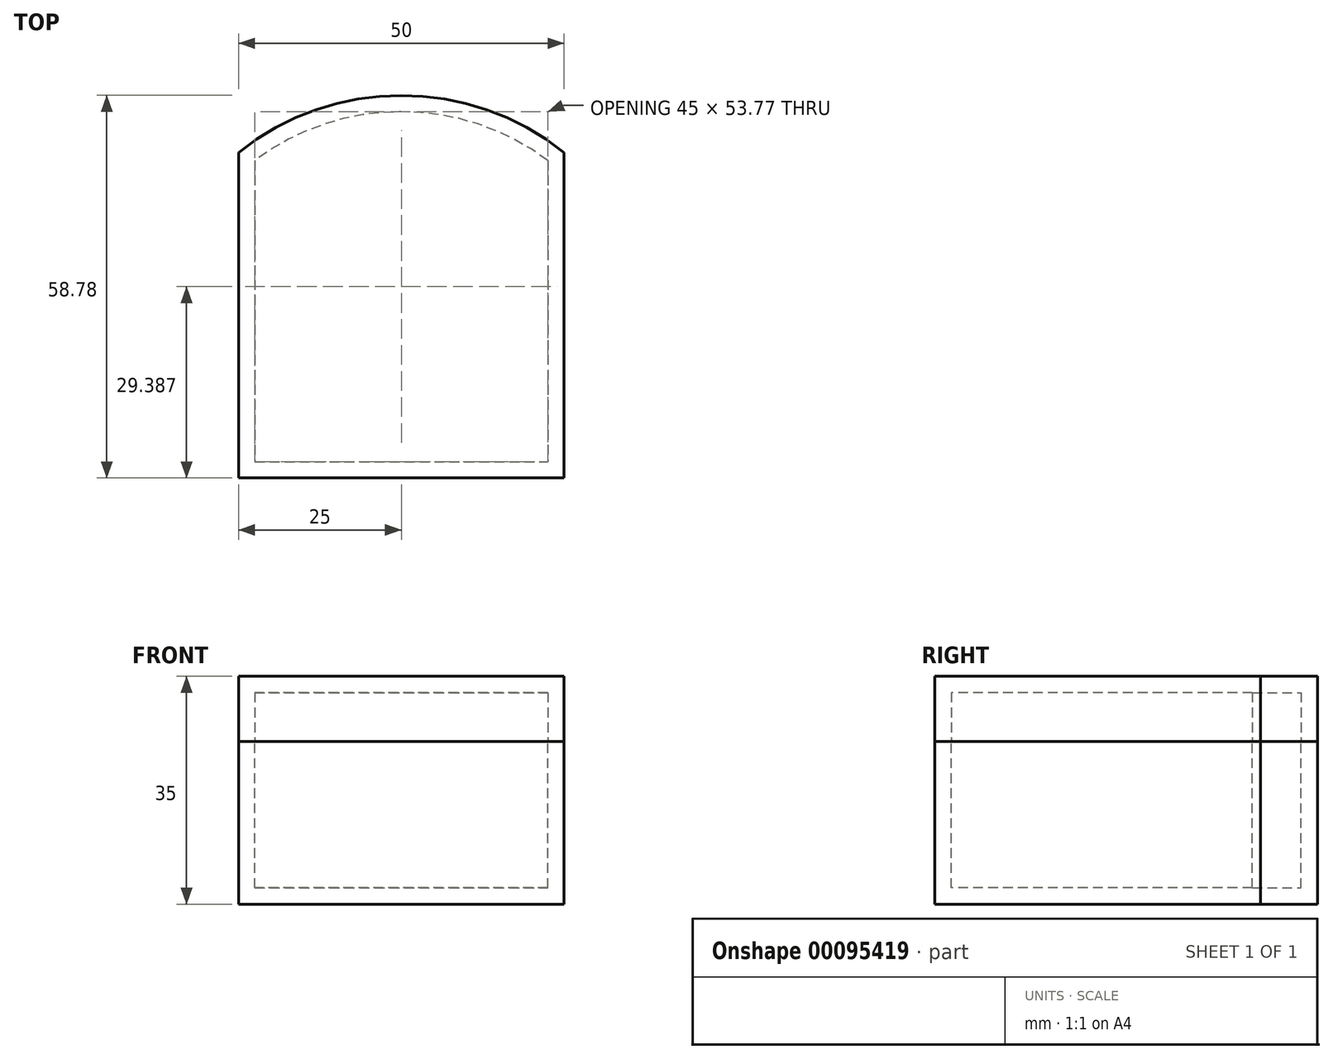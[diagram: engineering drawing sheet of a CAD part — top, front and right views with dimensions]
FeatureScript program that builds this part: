
annotation { "Feature Type Name" : "Feature", "Feature Type Description" : "" }
export const myFeature = defineFeature(function(context is Context, id is Id, definition is map)
    precondition{}
    {
        {
            var Q0;
            Q0=qCreatedBy(makeId("Top.planeOp"),FACE);
            var sketch = newSketch(context, id + "F0", { "sketchPlane" : qUnion([Q0])});
            skLineSegment(sketch, "E0.bottom", {"start": v(-25, 25) * mm, "end": v(25, 25) * mm});
            skLineSegment(sketch, "E0.top", {"start": v(-25, -25) * mm, "end": v(25, -25) * mm});
            skLineSegment(sketch, "E0.left", {"start": v(-25, 25) * mm, "end": v(-25, -25) * mm});
            skLineSegment(sketch, "E0.right", {"start": v(25, 25) * mm, "end": v(25, -25) * mm});
            skPoint(sketch, "E0.middle", {"position": v(0, 0) * mm});
            skArc(sketch, "E1", {"start": v(25, 25) * mm, "mid": v(0, 33.78) * mm, "end": v(-25, 25) * mm});
            skSolve(sketch);
        }
        {
            var Q0;
            Q0=makeQuery(id+"F0.imprint","IMPRINT",FACE,{"disambiguationData":[TD([[makeQuery(id+"F0.imprint","IMPRINT",EDGE,{"derivedFrom":sQuery(id+"F0.wireOp",EDGE,"E0.bottom")}),-1.0]])]});
            var Q1;
            Q1=makeQuery(id+"F0.imprint","IMPRINT",FACE,{"disambiguationData":[TD([[makeQuery(id+"F0.imprint","IMPRINT",EDGE,{"derivedFrom":sQuery(id+"F0.wireOp",EDGE,"E0.bottom")}),1.0]])]});
            extrude(context, id + "F1", {"entities" : qUnion([Q0, Q1]), "oppositeDirection" : true, "depth" : 25 * mm});
        }
        {
            var Q0;
            Q0=makeQuery(id+"F0.imprint","IMPRINT",FACE,{"disambiguationData":[TD([[makeQuery(id+"F0.imprint","IMPRINT",EDGE,{"derivedFrom":sQuery(id+"F0.wireOp",EDGE,"E0.bottom")}),1.0]])]});
            var Q1;
            Q1=makeQuery(id+"F0.imprint","IMPRINT",FACE,{"disambiguationData":[TD([[makeQuery(id+"F0.imprint","IMPRINT",EDGE,{"derivedFrom":sQuery(id+"F0.wireOp",EDGE,"E0.bottom")}),-1.0]])]});
            extrude(context, id + "F2", {"entities" : qUnion([Q0, Q1]), "depth" : 10 * mm});
        }
        {
            var Q0;
            Q0=makeQuery(id+"F1.opExtrude","CAP_FACE",FACE,{"disambiguationData":[OSD([sQuery(id+"F0.wireOp",EDGE,"E0.top"),sQuery(id+"F0.wireOp",EDGE,"E0.left"),sQuery(id+"F0.wireOp",EDGE,"E0.right"),sQuery(id+"F0.wireOp",EDGE,"E1")])],"isStart":true});
            var Q1;
            Q1=makeQuery(id+"F2.opExtrude","CAP_FACE",FACE,{"disambiguationData":[OSD([sQuery(id+"F0.wireOp",EDGE,"E0.top"),sQuery(id+"F0.wireOp",EDGE,"E0.left"),sQuery(id+"F0.wireOp",EDGE,"E0.right"),sQuery(id+"F0.wireOp",EDGE,"E1")])],"isStart":true});
            shell(context, id + "F3", {"entities" : qUnion([Q0, Q1]), "thickness" : 2.5 * mm});
        }
    });
